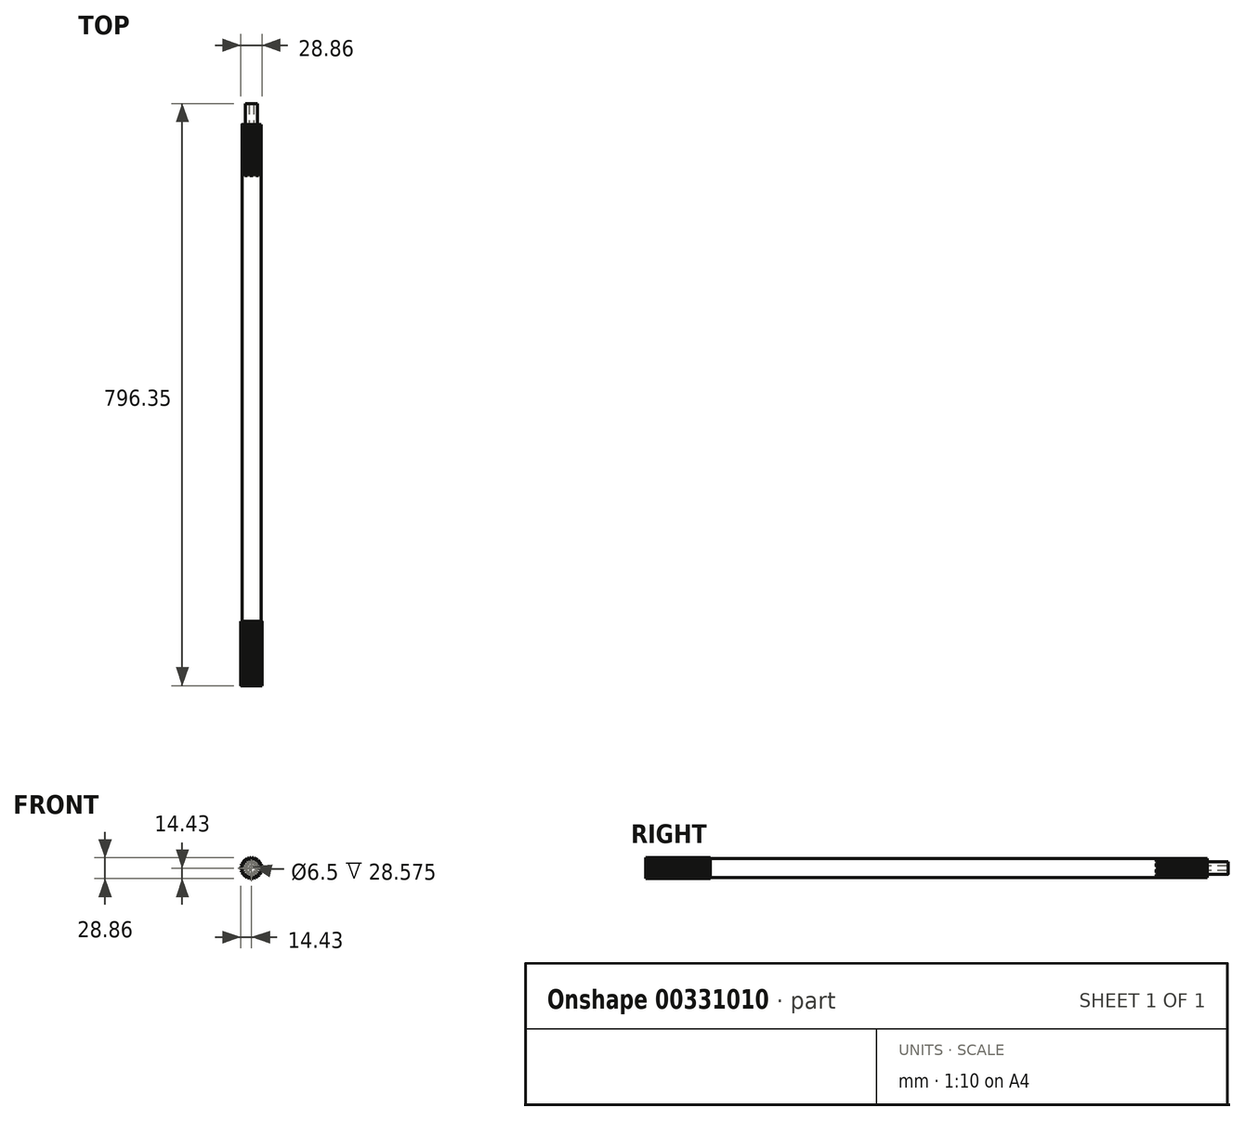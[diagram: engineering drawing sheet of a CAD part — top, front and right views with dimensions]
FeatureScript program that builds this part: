
annotation { "Feature Type Name" : "Feature", "Feature Type Description" : "" }
export const myFeature = defineFeature(function(context is Context, id is Id, definition is map)
    precondition{}
    {
        {
            var Q0;
            Q0=qCreatedBy(makeId("Front.planeOp"),FACE);
            var sketch = newSketch(context, id + "F0", { "sketchPlane" : qUnion([Q0])});
            skCircle(sketch, "E0", {"center": v(0, 0) * mm, "radius": 14.47 * mm, "construction": true});
            skLineSegment(sketch, "E1", {"start": v(-0.98, 14.47) * mm, "end": v(0.98, 14.47) * mm});
            skLineSegment(sketch, "E2", {"start": v(0.98, 14.47) * mm, "end": v(0.62, 12.5) * mm});
            skLineSegment(sketch, "E3", {"start": v(0.62, 12.5) * mm, "end": v(-0.62, 12.5) * mm});
            skLineSegment(sketch, "E4", {"start": v(-0.62, 12.5) * mm, "end": v(-0.98, 14.47) * mm});
            skPoint(sketch, "E5", {"position": v(0, 14.47) * mm});
            skPoint(sketch, "E6", {"position": v(0, 12.5) * mm});
            skLineSegment(sketch, "E7.1.0", {"start": v(-2.27, 14.32) * mm, "end": v(-2.18, 12.33) * mm});
            skPoint(sketch, "E7.1.1", {"position": v(-2.78, 12.2) * mm});
            skPoint(sketch, "E7.1.2", {"position": v(-3.22, 14.1) * mm});
            skLineSegment(sketch, "E7.1.3", {"start": v(-3.4, 12.06) * mm, "end": v(-4.17, 13.89) * mm});
            skLineSegment(sketch, "E7.1.4", {"start": v(-2.18, 12.33) * mm, "end": v(-3.4, 12.06) * mm});
            skLineSegment(sketch, "E7.1.5", {"start": v(-4.17, 13.89) * mm, "end": v(-2.27, 14.32) * mm});
            skLineSegment(sketch, "E7.2.0", {"start": v(-5.4, 13.46) * mm, "end": v(-4.87, 11.54) * mm});
            skPoint(sketch, "E7.2.1", {"position": v(-5.43, 11.27) * mm});
            skPoint(sketch, "E7.2.2", {"position": v(-6.28, 13.03) * mm});
            skLineSegment(sketch, "E7.2.3", {"start": v(-5.99, 11) * mm, "end": v(-7.16, 12.6) * mm});
            skLineSegment(sketch, "E7.2.4", {"start": v(-4.87, 11.54) * mm, "end": v(-5.99, 11) * mm});
            skLineSegment(sketch, "E7.2.5", {"start": v(-7.16, 12.6) * mm, "end": v(-5.4, 13.46) * mm});
            skLineSegment(sketch, "E7.3.0", {"start": v(-8.25, 11.92) * mm, "end": v(-7.31, 10.17) * mm});
            skPoint(sketch, "E7.3.1", {"position": v(-7.8, 9.78) * mm});
            skPoint(sketch, "E7.3.2", {"position": v(-9.02, 11.3) * mm});
            skLineSegment(sketch, "E7.3.3", {"start": v(-8.29, 9.4) * mm, "end": v(-9.78, 10.7) * mm});
            skLineSegment(sketch, "E7.3.4", {"start": v(-7.31, 10.17) * mm, "end": v(-8.29, 9.4) * mm});
            skLineSegment(sketch, "E7.3.5", {"start": v(-9.78, 10.7) * mm, "end": v(-8.25, 11.92) * mm});
            skLineSegment(sketch, "E7.4.0", {"start": v(-10.7, 9.78) * mm, "end": v(-9.4, 8.29) * mm});
            skPoint(sketch, "E7.4.1", {"position": v(-9.78, 7.8) * mm});
            skPoint(sketch, "E7.4.2", {"position": v(-11.3, 9.02) * mm});
            skLineSegment(sketch, "E7.4.3", {"start": v(-10.17, 7.31) * mm, "end": v(-11.92, 8.25) * mm});
            skLineSegment(sketch, "E7.4.4", {"start": v(-9.4, 8.29) * mm, "end": v(-10.17, 7.31) * mm});
            skLineSegment(sketch, "E7.4.5", {"start": v(-11.92, 8.25) * mm, "end": v(-10.7, 9.78) * mm});
            skLineSegment(sketch, "E7.5.0", {"start": v(-12.6, 7.16) * mm, "end": v(-11, 5.99) * mm});
            skPoint(sketch, "E7.5.1", {"position": v(-11.27, 5.43) * mm});
            skPoint(sketch, "E7.5.2", {"position": v(-13.03, 6.28) * mm});
            skLineSegment(sketch, "E7.5.3", {"start": v(-11.54, 4.87) * mm, "end": v(-13.46, 5.4) * mm});
            skLineSegment(sketch, "E7.5.4", {"start": v(-11, 5.99) * mm, "end": v(-11.54, 4.87) * mm});
            skLineSegment(sketch, "E7.5.5", {"start": v(-13.46, 5.4) * mm, "end": v(-12.6, 7.16) * mm});
            skLineSegment(sketch, "E7.6.0", {"start": v(-13.89, 4.17) * mm, "end": v(-12.06, 3.4) * mm});
            skPoint(sketch, "E7.6.1", {"position": v(-12.2, 2.78) * mm});
            skPoint(sketch, "E7.6.2", {"position": v(-14.1, 3.22) * mm});
            skLineSegment(sketch, "E7.6.3", {"start": v(-12.33, 2.18) * mm, "end": v(-14.32, 2.27) * mm});
            skLineSegment(sketch, "E7.6.4", {"start": v(-12.06, 3.4) * mm, "end": v(-12.33, 2.18) * mm});
            skLineSegment(sketch, "E7.6.5", {"start": v(-14.32, 2.27) * mm, "end": v(-13.89, 4.17) * mm});
            skLineSegment(sketch, "E7.7.0", {"start": v(-14.47, 0.98) * mm, "end": v(-12.5, 0.62) * mm});
            skPoint(sketch, "E7.7.1", {"position": v(-12.5, 0) * mm});
            skPoint(sketch, "E7.7.2", {"position": v(-14.47, 0) * mm});
            skLineSegment(sketch, "E7.7.3", {"start": v(-12.5, -0.62) * mm, "end": v(-14.47, -0.98) * mm});
            skLineSegment(sketch, "E7.7.4", {"start": v(-12.5, 0.62) * mm, "end": v(-12.5, -0.62) * mm});
            skLineSegment(sketch, "E7.7.5", {"start": v(-14.47, -0.98) * mm, "end": v(-14.47, 0.98) * mm});
            skLineSegment(sketch, "E7.8.0", {"start": v(-14.32, -2.27) * mm, "end": v(-12.33, -2.18) * mm});
            skPoint(sketch, "E7.8.1", {"position": v(-12.2, -2.78) * mm});
            skPoint(sketch, "E7.8.2", {"position": v(-14.1, -3.22) * mm});
            skLineSegment(sketch, "E7.8.3", {"start": v(-12.06, -3.4) * mm, "end": v(-13.89, -4.17) * mm});
            skLineSegment(sketch, "E7.8.4", {"start": v(-12.33, -2.18) * mm, "end": v(-12.06, -3.4) * mm});
            skLineSegment(sketch, "E7.8.5", {"start": v(-13.89, -4.17) * mm, "end": v(-14.32, -2.27) * mm});
            skLineSegment(sketch, "E7.9.0", {"start": v(-13.46, -5.4) * mm, "end": v(-11.54, -4.87) * mm});
            skPoint(sketch, "E7.9.1", {"position": v(-11.27, -5.43) * mm});
            skPoint(sketch, "E7.9.2", {"position": v(-13.03, -6.28) * mm});
            skLineSegment(sketch, "E7.9.3", {"start": v(-11, -5.99) * mm, "end": v(-12.6, -7.16) * mm});
            skLineSegment(sketch, "E7.9.4", {"start": v(-11.54, -4.87) * mm, "end": v(-11, -5.99) * mm});
            skLineSegment(sketch, "E7.9.5", {"start": v(-12.6, -7.16) * mm, "end": v(-13.46, -5.4) * mm});
            skLineSegment(sketch, "E7.10.0", {"start": v(-11.92, -8.25) * mm, "end": v(-10.17, -7.31) * mm});
            skPoint(sketch, "E7.10.1", {"position": v(-9.78, -7.8) * mm});
            skPoint(sketch, "E7.10.2", {"position": v(-11.3, -9.02) * mm});
            skLineSegment(sketch, "E7.10.3", {"start": v(-9.4, -8.29) * mm, "end": v(-10.7, -9.78) * mm});
            skLineSegment(sketch, "E7.10.4", {"start": v(-10.17, -7.31) * mm, "end": v(-9.4, -8.29) * mm});
            skLineSegment(sketch, "E7.10.5", {"start": v(-10.7, -9.78) * mm, "end": v(-11.92, -8.25) * mm});
            skLineSegment(sketch, "E7.11.0", {"start": v(-9.78, -10.7) * mm, "end": v(-8.29, -9.4) * mm});
            skPoint(sketch, "E7.11.1", {"position": v(-7.8, -9.78) * mm});
            skPoint(sketch, "E7.11.2", {"position": v(-9.02, -11.3) * mm});
            skLineSegment(sketch, "E7.11.3", {"start": v(-7.31, -10.17) * mm, "end": v(-8.25, -11.92) * mm});
            skLineSegment(sketch, "E7.11.4", {"start": v(-8.29, -9.4) * mm, "end": v(-7.31, -10.17) * mm});
            skLineSegment(sketch, "E7.11.5", {"start": v(-8.25, -11.92) * mm, "end": v(-9.78, -10.7) * mm});
            skLineSegment(sketch, "E7.12.0", {"start": v(-7.16, -12.6) * mm, "end": v(-5.99, -11) * mm});
            skPoint(sketch, "E7.12.1", {"position": v(-5.43, -11.27) * mm});
            skPoint(sketch, "E7.12.2", {"position": v(-6.28, -13.03) * mm});
            skLineSegment(sketch, "E7.12.3", {"start": v(-4.87, -11.54) * mm, "end": v(-5.4, -13.46) * mm});
            skLineSegment(sketch, "E7.12.4", {"start": v(-5.99, -11) * mm, "end": v(-4.87, -11.54) * mm});
            skLineSegment(sketch, "E7.12.5", {"start": v(-5.4, -13.46) * mm, "end": v(-7.16, -12.6) * mm});
            skLineSegment(sketch, "E7.13.0", {"start": v(-4.17, -13.89) * mm, "end": v(-3.4, -12.06) * mm});
            skPoint(sketch, "E7.13.1", {"position": v(-2.78, -12.2) * mm});
            skPoint(sketch, "E7.13.2", {"position": v(-3.22, -14.1) * mm});
            skLineSegment(sketch, "E7.13.3", {"start": v(-2.18, -12.33) * mm, "end": v(-2.27, -14.32) * mm});
            skLineSegment(sketch, "E7.13.4", {"start": v(-3.4, -12.06) * mm, "end": v(-2.18, -12.33) * mm});
            skLineSegment(sketch, "E7.13.5", {"start": v(-2.27, -14.32) * mm, "end": v(-4.17, -13.89) * mm});
            skLineSegment(sketch, "E7.14.0", {"start": v(-0.98, -14.47) * mm, "end": v(-0.62, -12.5) * mm});
            skPoint(sketch, "E7.14.1", {"position": v(0, -12.5) * mm});
            skPoint(sketch, "E7.14.2", {"position": v(0, -14.47) * mm});
            skLineSegment(sketch, "E7.14.3", {"start": v(0.62, -12.5) * mm, "end": v(0.98, -14.47) * mm});
            skLineSegment(sketch, "E7.14.4", {"start": v(-0.62, -12.5) * mm, "end": v(0.62, -12.5) * mm});
            skLineSegment(sketch, "E7.14.5", {"start": v(0.98, -14.47) * mm, "end": v(-0.98, -14.47) * mm});
            skLineSegment(sketch, "E7.15.0", {"start": v(2.27, -14.32) * mm, "end": v(2.18, -12.33) * mm});
            skPoint(sketch, "E7.15.1", {"position": v(2.78, -12.2) * mm});
            skPoint(sketch, "E7.15.2", {"position": v(3.22, -14.1) * mm});
            skLineSegment(sketch, "E7.15.3", {"start": v(3.4, -12.06) * mm, "end": v(4.17, -13.89) * mm});
            skLineSegment(sketch, "E7.15.4", {"start": v(2.18, -12.33) * mm, "end": v(3.4, -12.06) * mm});
            skLineSegment(sketch, "E7.15.5", {"start": v(4.17, -13.89) * mm, "end": v(2.27, -14.32) * mm});
            skLineSegment(sketch, "E7.16.0", {"start": v(5.4, -13.46) * mm, "end": v(4.87, -11.54) * mm});
            skPoint(sketch, "E7.16.1", {"position": v(5.43, -11.27) * mm});
            skPoint(sketch, "E7.16.2", {"position": v(6.28, -13.03) * mm});
            skLineSegment(sketch, "E7.16.3", {"start": v(5.99, -11) * mm, "end": v(7.16, -12.6) * mm});
            skLineSegment(sketch, "E7.16.4", {"start": v(4.87, -11.54) * mm, "end": v(5.99, -11) * mm});
            skLineSegment(sketch, "E7.16.5", {"start": v(7.16, -12.6) * mm, "end": v(5.4, -13.46) * mm});
            skLineSegment(sketch, "E7.17.0", {"start": v(8.25, -11.92) * mm, "end": v(7.31, -10.17) * mm});
            skPoint(sketch, "E7.17.1", {"position": v(7.8, -9.78) * mm});
            skPoint(sketch, "E7.17.2", {"position": v(9.02, -11.3) * mm});
            skLineSegment(sketch, "E7.17.3", {"start": v(8.29, -9.4) * mm, "end": v(9.78, -10.7) * mm});
            skLineSegment(sketch, "E7.17.4", {"start": v(7.31, -10.17) * mm, "end": v(8.29, -9.4) * mm});
            skLineSegment(sketch, "E7.17.5", {"start": v(9.78, -10.7) * mm, "end": v(8.25, -11.92) * mm});
            skLineSegment(sketch, "E7.18.0", {"start": v(10.7, -9.78) * mm, "end": v(9.4, -8.29) * mm});
            skPoint(sketch, "E7.18.1", {"position": v(9.78, -7.8) * mm});
            skPoint(sketch, "E7.18.2", {"position": v(11.3, -9.02) * mm});
            skLineSegment(sketch, "E7.18.3", {"start": v(10.17, -7.31) * mm, "end": v(11.92, -8.25) * mm});
            skLineSegment(sketch, "E7.18.4", {"start": v(9.4, -8.29) * mm, "end": v(10.17, -7.31) * mm});
            skLineSegment(sketch, "E7.18.5", {"start": v(11.92, -8.25) * mm, "end": v(10.7, -9.78) * mm});
            skLineSegment(sketch, "E7.19.0", {"start": v(12.6, -7.16) * mm, "end": v(11, -5.99) * mm});
            skPoint(sketch, "E7.19.1", {"position": v(11.27, -5.43) * mm});
            skPoint(sketch, "E7.19.2", {"position": v(13.03, -6.28) * mm});
            skLineSegment(sketch, "E7.19.3", {"start": v(11.54, -4.87) * mm, "end": v(13.46, -5.4) * mm});
            skLineSegment(sketch, "E7.19.4", {"start": v(11, -5.99) * mm, "end": v(11.54, -4.87) * mm});
            skLineSegment(sketch, "E7.19.5", {"start": v(13.46, -5.4) * mm, "end": v(12.6, -7.16) * mm});
            skLineSegment(sketch, "E7.20.0", {"start": v(13.89, -4.17) * mm, "end": v(12.06, -3.4) * mm});
            skPoint(sketch, "E7.20.1", {"position": v(12.2, -2.78) * mm});
            skPoint(sketch, "E7.20.2", {"position": v(14.1, -3.22) * mm});
            skLineSegment(sketch, "E7.20.3", {"start": v(12.33, -2.18) * mm, "end": v(14.32, -2.27) * mm});
            skLineSegment(sketch, "E7.20.4", {"start": v(12.06, -3.4) * mm, "end": v(12.33, -2.18) * mm});
            skLineSegment(sketch, "E7.20.5", {"start": v(14.32, -2.27) * mm, "end": v(13.89, -4.17) * mm});
            skLineSegment(sketch, "E7.21.0", {"start": v(14.47, -0.98) * mm, "end": v(12.5, -0.62) * mm});
            skPoint(sketch, "E7.21.1", {"position": v(12.5, 0) * mm});
            skPoint(sketch, "E7.21.2", {"position": v(14.47, 0) * mm});
            skLineSegment(sketch, "E7.21.3", {"start": v(12.5, 0.62) * mm, "end": v(14.47, 0.98) * mm});
            skLineSegment(sketch, "E7.21.4", {"start": v(12.5, -0.62) * mm, "end": v(12.5, 0.62) * mm});
            skLineSegment(sketch, "E7.21.5", {"start": v(14.47, 0.98) * mm, "end": v(14.47, -0.98) * mm});
            skLineSegment(sketch, "E7.22.0", {"start": v(14.32, 2.27) * mm, "end": v(12.33, 2.18) * mm});
            skPoint(sketch, "E7.22.1", {"position": v(12.2, 2.78) * mm});
            skPoint(sketch, "E7.22.2", {"position": v(14.1, 3.22) * mm});
            skLineSegment(sketch, "E7.22.3", {"start": v(12.06, 3.4) * mm, "end": v(13.89, 4.17) * mm});
            skLineSegment(sketch, "E7.22.4", {"start": v(12.33, 2.18) * mm, "end": v(12.06, 3.4) * mm});
            skLineSegment(sketch, "E7.22.5", {"start": v(13.89, 4.17) * mm, "end": v(14.32, 2.27) * mm});
            skLineSegment(sketch, "E7.23.0", {"start": v(13.46, 5.4) * mm, "end": v(11.54, 4.87) * mm});
            skPoint(sketch, "E7.23.1", {"position": v(11.27, 5.43) * mm});
            skPoint(sketch, "E7.23.2", {"position": v(13.03, 6.28) * mm});
            skLineSegment(sketch, "E7.23.3", {"start": v(11, 5.99) * mm, "end": v(12.6, 7.16) * mm});
            skLineSegment(sketch, "E7.23.4", {"start": v(11.54, 4.87) * mm, "end": v(11, 5.99) * mm});
            skLineSegment(sketch, "E7.23.5", {"start": v(12.6, 7.16) * mm, "end": v(13.46, 5.4) * mm});
            skLineSegment(sketch, "E7.24.0", {"start": v(11.92, 8.25) * mm, "end": v(10.17, 7.31) * mm});
            skPoint(sketch, "E7.24.1", {"position": v(9.78, 7.8) * mm});
            skPoint(sketch, "E7.24.2", {"position": v(11.3, 9.02) * mm});
            skLineSegment(sketch, "E7.24.3", {"start": v(9.4, 8.29) * mm, "end": v(10.7, 9.78) * mm});
            skLineSegment(sketch, "E7.24.4", {"start": v(10.17, 7.31) * mm, "end": v(9.4, 8.29) * mm});
            skLineSegment(sketch, "E7.24.5", {"start": v(10.7, 9.78) * mm, "end": v(11.92, 8.25) * mm});
            skLineSegment(sketch, "E7.25.0", {"start": v(9.78, 10.7) * mm, "end": v(8.29, 9.4) * mm});
            skPoint(sketch, "E7.25.1", {"position": v(7.8, 9.78) * mm});
            skPoint(sketch, "E7.25.2", {"position": v(9.02, 11.3) * mm});
            skLineSegment(sketch, "E7.25.3", {"start": v(7.31, 10.17) * mm, "end": v(8.25, 11.92) * mm});
            skLineSegment(sketch, "E7.25.4", {"start": v(8.29, 9.4) * mm, "end": v(7.31, 10.17) * mm});
            skLineSegment(sketch, "E7.25.5", {"start": v(8.25, 11.92) * mm, "end": v(9.78, 10.7) * mm});
            skLineSegment(sketch, "E7.26.0", {"start": v(7.16, 12.6) * mm, "end": v(5.99, 11) * mm});
            skPoint(sketch, "E7.26.1", {"position": v(5.43, 11.27) * mm});
            skPoint(sketch, "E7.26.2", {"position": v(6.28, 13.03) * mm});
            skLineSegment(sketch, "E7.26.3", {"start": v(4.87, 11.54) * mm, "end": v(5.4, 13.46) * mm});
            skLineSegment(sketch, "E7.26.4", {"start": v(5.99, 11) * mm, "end": v(4.87, 11.54) * mm});
            skLineSegment(sketch, "E7.26.5", {"start": v(5.4, 13.46) * mm, "end": v(7.16, 12.6) * mm});
            skLineSegment(sketch, "E7.27.0", {"start": v(4.17, 13.89) * mm, "end": v(3.4, 12.06) * mm});
            skPoint(sketch, "E7.27.1", {"position": v(2.78, 12.2) * mm});
            skPoint(sketch, "E7.27.2", {"position": v(3.22, 14.1) * mm});
            skLineSegment(sketch, "E7.27.3", {"start": v(2.18, 12.33) * mm, "end": v(2.27, 14.32) * mm});
            skLineSegment(sketch, "E7.27.4", {"start": v(3.4, 12.06) * mm, "end": v(2.18, 12.33) * mm});
            skLineSegment(sketch, "E7.27.5", {"start": v(2.27, 14.32) * mm, "end": v(4.17, 13.89) * mm});
            skSolve(sketch);
        }
        {
            var Q0;
            Q0=qCreatedBy(makeId("Front.planeOp"),FACE);
            var sketch = newSketch(context, id + "F1", { "sketchPlane" : qUnion([Q0])});
            skCircle(sketch, "E8", {"center": v(0, 0) * mm, "radius": 14.47 * mm});
            skSolve(sketch);
        }
        {
            var Q0;
            Q0 = qSketchRegion(id + "F1", true);
            extrude(context, id + "F2", {"entities" : qUnion([Q0]), "depth" : 88.32 * mm});
        }
        {
            var Q0;
            Q0 = qSketchRegion(id + "F0", true);
            extrude(context, id + "F3", {"entities" : qUnion([Q0]), "operationType" : NewBodyOperationType.REMOVE, "depth" : 88.32 * mm});
        }
        {
            var Q0;
            Q0=qCreatedBy(makeId("Front.planeOp"),FACE);
            var Q1;
            Q1=makeQuery(id+"F2.opExtrude","CAP_FACE",FACE,{"disambiguationData":[OSD([sQuery(id+"F1.wireOp",EDGE,"E8")])],"isStart":true});
            cPlane(context, id + "F4", {"entities" : qUnion([Q0, Q1]), "cplaneType" : CPlaneType.MID_PLANE, "offset" : 25.4 * mm, "width" : 152.4 * mm, "height" : 152.4 * mm});
        }
        {
            var Q0;
            Q0=qCreatedBy(id+"F4.planeOp",FACE);
            var sketch = newSketch(context, id + "F5", { "sketchPlane" : qUnion([Q0])});
            skCircle(sketch, "E9", {"center": v(0, 0) * mm, "radius": 13.08 * mm});
            skSolve(sketch);
        }
        {
            var Q0;
            Q0 = qSketchRegion(id + "F5", true);
            extrude(context, id + "F6", {"entities" : qUnion([Q0]), "operationType" : NewBodyOperationType.ADD, "oppositeDirection" : true, "depth" : 279.4 * mm});
        }
        {
            var Q0;
            Q0=makeQuery(id+"F6.opExtrude","CAP_FACE",FACE,{"disambiguationData":[OSD([sQuery(id+"F5.wireOp",EDGE,"E9")])],"isStart":false});
            cPlane(context, id + "F7", {"entities" : qUnion([Q0]), "cplaneType" : CPlaneType.OFFSET, "offset" : 0 * mm, "width" : 152.4 * mm, "height" : 152.4 * mm});
        }
        {
            var Q0;
            Q0=qCreatedBy(id+"F7.planeOp",FACE);
            var sketch = newSketch(context, id + "F8", { "sketchPlane" : qUnion([Q0])});
            skCircle(sketch, "E10", {"center": v(0, 0) * mm, "radius": 13.08 * mm});
            skSolve(sketch);
        }
        {
            var Q0;
            Q0 = qSketchRegion(id + "F8", true);
            extrude(context, id + "F9", {"entities" : qUnion([Q0]), "operationType" : NewBodyOperationType.ADD, "depth" : 276.22 * mm});
        }
        {
            var Q0;
            Q0=makeQuery(id+"F9.opExtrude","CAP_FACE",FACE,{"disambiguationData":[OSD([sQuery(id+"F8.wireOp",EDGE,"E10")])],"isStart":false});
            cPlane(context, id + "F10", {"entities" : qUnion([Q0]), "cplaneType" : CPlaneType.OFFSET, "offset" : 0 * mm, "width" : 152.4 * mm, "height" : 152.4 * mm});
        }
        {
            var Q0;
            Q0=qCreatedBy(id+"F10.planeOp",FACE);
            var sketch = newSketch(context, id + "F11", { "sketchPlane" : qUnion([Q0])});
            skCircle(sketch, "E11", {"center": v(0, 0) * mm, "radius": 13.08 * mm});
            skSolve(sketch);
        }
        {
            var Q0;
            Q0 = qSketchRegion(id + "F11", true);
            extrude(context, id + "F12", {"entities" : qUnion([Q0]), "operationType" : NewBodyOperationType.ADD, "depth" : 53.97 * mm});
        }
        {
            var Q0;
            Q0=makeQuery(id+"F12.opExtrude","CAP_FACE",FACE,{"disambiguationData":[OSD([sQuery(id+"F11.wireOp",EDGE,"E11")])],"isStart":false});
            cPlane(context, id + "F13", {"entities" : qUnion([Q0]), "cplaneType" : CPlaneType.OFFSET, "offset" : 0 * mm, "width" : 152.4 * mm, "height" : 152.4 * mm});
        }
        {
            var Q0;
            Q0=qCreatedBy(id+"F13.planeOp",FACE);
            var sketch = newSketch(context, id + "F14", { "sketchPlane" : qUnion([Q0])});
            skCircle(sketch, "E12", {"center": v(0, 0) * mm, "radius": 13.08 * mm});
            skSolve(sketch);
        }
        {
            var Q0;
            Q0 = qSketchRegion(id + "F14", true);
            extrude(context, id + "F15", {"entities" : qUnion([Q0]), "operationType" : NewBodyOperationType.ADD, "depth" : 69.85 * mm});
        }
        {
            var Q0;
            Q0=qCreatedBy(id+"F13.planeOp",FACE);
            var sketch = newSketch(context, id + "F16", { "sketchPlane" : qUnion([Q0])});
            skLineSegment(sketch, "E13", {"start": v(-1.98, 13.08) * mm, "end": v(1.98, 13.08) * mm});
            skLineSegment(sketch, "E14", {"start": v(1.98, 13.08) * mm, "end": v(0.98, 5.69) * mm});
            skLineSegment(sketch, "E15", {"start": v(0.98, 5.69) * mm, "end": v(-0.98, 5.69) * mm});
            skLineSegment(sketch, "E16", {"start": v(-0.98, 5.69) * mm, "end": v(-1.98, 13.08) * mm});
            skPoint(sketch, "E17", {"position": v(0, 13.08) * mm});
            skPoint(sketch, "E18", {"position": v(0, 5.69) * mm});
            skPoint(sketch, "E19.1.0", {"position": v(-7.69, 10.58) * mm});
            skLineSegment(sketch, "E19.1.1", {"start": v(-4.14, 4.03) * mm, "end": v(-9.3, 9.42) * mm});
            skPoint(sketch, "E19.1.2", {"position": v(-3.34, 4.6) * mm});
            skLineSegment(sketch, "E19.1.3", {"start": v(-2.55, 5.18) * mm, "end": v(-4.14, 4.03) * mm});
            skLineSegment(sketch, "E19.1.4", {"start": v(-6.09, 11.75) * mm, "end": v(-2.55, 5.18) * mm});
            skLineSegment(sketch, "E19.1.5", {"start": v(-9.3, 9.42) * mm, "end": v(-6.09, 11.75) * mm});
            skPoint(sketch, "E19.2.0", {"position": v(-12.44, 4.04) * mm});
            skLineSegment(sketch, "E19.2.1", {"start": v(-5.71, 0.83) * mm, "end": v(-13.05, 2.16) * mm});
            skPoint(sketch, "E19.2.2", {"position": v(-5.41, 1.76) * mm});
            skLineSegment(sketch, "E19.2.3", {"start": v(-5.1, 2.69) * mm, "end": v(-5.71, 0.83) * mm});
            skLineSegment(sketch, "E19.2.4", {"start": v(-11.83, 5.93) * mm, "end": v(-5.1, 2.69) * mm});
            skLineSegment(sketch, "E19.2.5", {"start": v(-13.05, 2.16) * mm, "end": v(-11.83, 5.93) * mm});
            skPoint(sketch, "E19.3.0", {"position": v(-12.44, -4.04) * mm});
            skLineSegment(sketch, "E19.3.1", {"start": v(-5.1, -2.69) * mm, "end": v(-11.83, -5.93) * mm});
            skPoint(sketch, "E19.3.2", {"position": v(-5.41, -1.76) * mm});
            skLineSegment(sketch, "E19.3.3", {"start": v(-5.71, -0.83) * mm, "end": v(-5.1, -2.69) * mm});
            skLineSegment(sketch, "E19.3.4", {"start": v(-13.05, -2.16) * mm, "end": v(-5.71, -0.83) * mm});
            skLineSegment(sketch, "E19.3.5", {"start": v(-11.83, -5.93) * mm, "end": v(-13.05, -2.16) * mm});
            skPoint(sketch, "E19.4.0", {"position": v(-7.69, -10.58) * mm});
            skLineSegment(sketch, "E19.4.1", {"start": v(-2.55, -5.18) * mm, "end": v(-6.09, -11.75) * mm});
            skPoint(sketch, "E19.4.2", {"position": v(-3.34, -4.6) * mm});
            skLineSegment(sketch, "E19.4.3", {"start": v(-4.14, -4.03) * mm, "end": v(-2.55, -5.18) * mm});
            skLineSegment(sketch, "E19.4.4", {"start": v(-9.3, -9.42) * mm, "end": v(-4.14, -4.03) * mm});
            skLineSegment(sketch, "E19.4.5", {"start": v(-6.09, -11.75) * mm, "end": v(-9.3, -9.42) * mm});
            skPoint(sketch, "E19.5.0", {"position": v(0, -13.08) * mm});
            skLineSegment(sketch, "E19.5.1", {"start": v(0.98, -5.69) * mm, "end": v(1.98, -13.08) * mm});
            skPoint(sketch, "E19.5.2", {"position": v(0, -5.69) * mm});
            skLineSegment(sketch, "E19.5.3", {"start": v(-0.98, -5.69) * mm, "end": v(0.98, -5.69) * mm});
            skLineSegment(sketch, "E19.5.4", {"start": v(-1.98, -13.08) * mm, "end": v(-0.98, -5.69) * mm});
            skLineSegment(sketch, "E19.5.5", {"start": v(1.98, -13.08) * mm, "end": v(-1.98, -13.08) * mm});
            skPoint(sketch, "E19.6.0", {"position": v(7.69, -10.58) * mm});
            skLineSegment(sketch, "E19.6.1", {"start": v(4.14, -4.03) * mm, "end": v(9.3, -9.42) * mm});
            skPoint(sketch, "E19.6.2", {"position": v(3.34, -4.6) * mm});
            skLineSegment(sketch, "E19.6.3", {"start": v(2.55, -5.18) * mm, "end": v(4.14, -4.03) * mm});
            skLineSegment(sketch, "E19.6.4", {"start": v(6.09, -11.75) * mm, "end": v(2.55, -5.18) * mm});
            skLineSegment(sketch, "E19.6.5", {"start": v(9.3, -9.42) * mm, "end": v(6.09, -11.75) * mm});
            skPoint(sketch, "E19.7.0", {"position": v(12.44, -4.04) * mm});
            skLineSegment(sketch, "E19.7.1", {"start": v(5.71, -0.83) * mm, "end": v(13.05, -2.16) * mm});
            skPoint(sketch, "E19.7.2", {"position": v(5.41, -1.76) * mm});
            skLineSegment(sketch, "E19.7.3", {"start": v(5.1, -2.69) * mm, "end": v(5.71, -0.83) * mm});
            skLineSegment(sketch, "E19.7.4", {"start": v(11.83, -5.93) * mm, "end": v(5.1, -2.69) * mm});
            skLineSegment(sketch, "E19.7.5", {"start": v(13.05, -2.16) * mm, "end": v(11.83, -5.93) * mm});
            skPoint(sketch, "E19.8.0", {"position": v(12.44, 4.04) * mm});
            skLineSegment(sketch, "E19.8.1", {"start": v(5.1, 2.69) * mm, "end": v(11.83, 5.93) * mm});
            skPoint(sketch, "E19.8.2", {"position": v(5.41, 1.76) * mm});
            skLineSegment(sketch, "E19.8.3", {"start": v(5.71, 0.83) * mm, "end": v(5.1, 2.69) * mm});
            skLineSegment(sketch, "E19.8.4", {"start": v(13.05, 2.16) * mm, "end": v(5.71, 0.83) * mm});
            skLineSegment(sketch, "E19.8.5", {"start": v(11.83, 5.93) * mm, "end": v(13.05, 2.16) * mm});
            skPoint(sketch, "E19.9.0", {"position": v(7.69, 10.58) * mm});
            skLineSegment(sketch, "E19.9.1", {"start": v(2.55, 5.18) * mm, "end": v(6.09, 11.75) * mm});
            skPoint(sketch, "E19.9.2", {"position": v(3.34, 4.6) * mm});
            skLineSegment(sketch, "E19.9.3", {"start": v(4.14, 4.03) * mm, "end": v(2.55, 5.18) * mm});
            skLineSegment(sketch, "E19.9.4", {"start": v(9.3, 9.42) * mm, "end": v(4.14, 4.03) * mm});
            skLineSegment(sketch, "E19.9.5", {"start": v(6.09, 11.75) * mm, "end": v(9.3, 9.42) * mm});
            skPoint(sketch, "E19.center", {"position": v(0, 0) * mm});
            skSolve(sketch);
        }
        {
            var Q0;
            Q0 = qSketchRegion(id + "F16", true);
            extrude(context, id + "F17", {"entities" : qUnion([Q0]), "operationType" : NewBodyOperationType.REMOVE, "depth" : 69.85 * mm});
        }
        {
            var Q0;
            Q0=makeQuery(id+"F15.opExtrude","CAP_FACE",FACE,{"disambiguationData":[OSD([sQuery(id+"F14.wireOp",EDGE,"E12")])],"isStart":false});
            cPlane(context, id + "F18", {"entities" : qUnion([Q0]), "cplaneType" : CPlaneType.OFFSET, "offset" : 0 * mm, "width" : 152.4 * mm, "height" : 152.4 * mm});
        }
        {
            var Q0;
            Q0=qCreatedBy(id+"F18.planeOp",FACE);
            var sketch = newSketch(context, id + "F19", { "sketchPlane" : qUnion([Q0])});
            skCircle(sketch, "E20", {"center": v(0, 0) * mm, "radius": 8.46 * mm});
            skCircle(sketch, "E21", {"center": v(0, 0) * mm, "radius": 3.25 * mm});
            skSolve(sketch);
        }
        {
            var Q0;
            Q0 = qSketchRegion(id + "F19", true);
            extrude(context, id + "F20", {"entities" : qUnion([Q0]), "operationType" : NewBodyOperationType.ADD, "depth" : 28.57 * mm});
        }
    });
